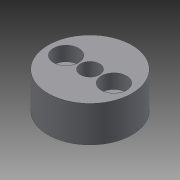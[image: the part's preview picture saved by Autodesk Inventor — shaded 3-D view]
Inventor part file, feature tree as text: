
AUTODESK INVENTOR PART (.ipt)
format: ipt  version: 2014 (Build 180170000, 170)  size: 95,232 bytes
history: native  units: mm
features: extrude x2, sketch x2
ambient origin geometry x8: Origin, YZ Plane, XZ Plane, XY Plane, X Axis, Y Axis, Z Axis, Center Point
bodies: Solid1 (feature_tree)
feature tree (4):
  extrude  "Extrusion1"  Depth=8.0mm
  extrude  "Extrusion3"  Depth=6.0mm
  sketch  "Sketch1"  dims[d0=35.0mm d1=8.0mm]
  sketch  "Sketch3"  dims[d2=15.0mm d3=0.0mm d7=20.0mm d8=6.0mm d9=10.5mm d10=6.0mm d11=0.0mm]
